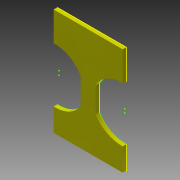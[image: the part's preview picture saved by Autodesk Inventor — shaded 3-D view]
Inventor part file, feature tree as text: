
AUTODESK INVENTOR PART (.ipt)
format: ipt  version: 2013 (Build 170138000, 138)  size: 253,952 bytes
history: native  units: mm
features: sketch x10, extrude x9, other x1
ambient origin geometry x8: Origin, YZ Plane, XZ Plane, XY Plane, X Axis, Y Axis, Z Axis, Center Point
feature tree (20):
  other  "ソリッド1"
  extrude  "押し出し1"  Depth=25.0mm
  sketch  "スケッチ2"
  extrude  "押し出し3"  Depth=79.965mm
  extrude  "押し出し4"  Depth=34.641mm
  extrude  "押し出し5"  Depth=90.0mm
  extrude  "押し出し6"  Depth=94.0mm
  extrude  "押し出し7"  Depth=31.0mm
  extrude  "押し出し8"  Depth=94.0mm
  extrude  "押し出し9"  Depth=40.0mm
  extrude  "押し出し10"  Depth=90.0mm
  sketch  "スケッチ1"
  sketch  "スケッチ3"
  sketch  "スケッチ4"
  sketch  "スケッチ5"
  sketch  "スケッチ6"
  sketch  "スケッチ7"
  sketch  "スケッチ8"
  sketch  "スケッチ9"
  sketch  "スケッチ10"
